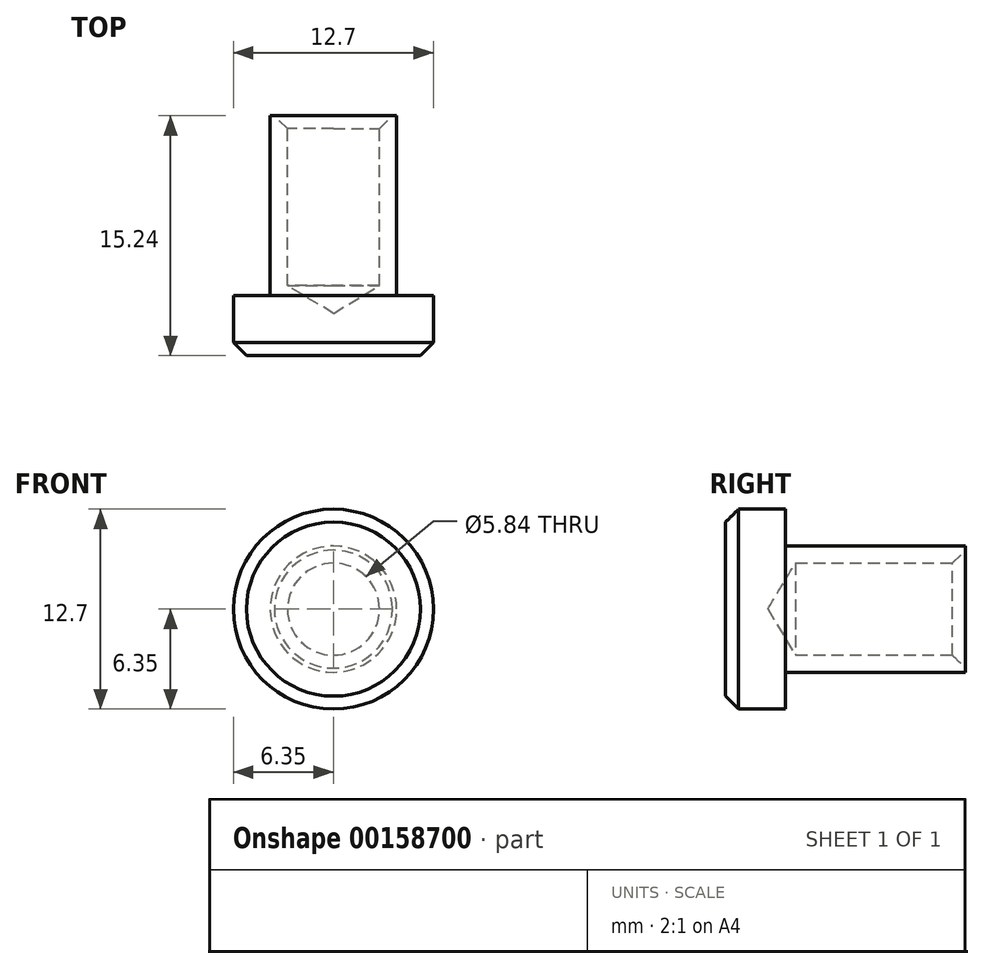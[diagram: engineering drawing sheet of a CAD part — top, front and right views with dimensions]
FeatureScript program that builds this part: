
annotation { "Feature Type Name" : "Feature", "Feature Type Description" : "" }
export const myFeature = defineFeature(function(context is Context, id is Id, definition is map)
    precondition{}
    {
        {
            var Q0;
            Q0=qCreatedBy(makeId("Right.planeOp"),FACE);
            var sketch = newSketch(context, id + "F0", { "sketchPlane" : qUnion([Q0])});
            skLineSegment(sketch, "E0", {"start": v(0, 0) * mm, "end": v(0, 6.35) * mm});
            skLineSegment(sketch, "E1", {"start": v(0, 6.35) * mm, "end": v(3.81, 6.35) * mm});
            skLineSegment(sketch, "E2", {"start": v(3.81, 6.35) * mm, "end": v(3.81, 4.01) * mm});
            skLineSegment(sketch, "E3", {"start": v(3.8, 4.01) * mm, "end": v(15.24, 4.01) * mm});
            skLineSegment(sketch, "E4", {"start": v(15.24, 4.01) * mm, "end": v(15.24, 2.92) * mm});
            skLineSegment(sketch, "E5", {"start": v(15.24, 2.92) * mm, "end": v(4.44, 2.92) * mm});
            skLineSegment(sketch, "E6", {"start": v(4.44, 2.92) * mm, "end": v(2.69, 0) * mm});
            skLineSegment(sketch, "E7", {"start": v(2.69, 0) * mm, "end": v(0, 0) * mm});
            skSolve(sketch);
        }
        {
            var Q0;
            Q0=makeQuery(id+"F0.imprint","IMPRINT",FACE,{"disambiguationData":[TD([[makeQuery(id+"F0.imprint","IMPRINT",EDGE,{"derivedFrom":sQuery(id+"F0.wireOp",EDGE,"E0")}),-1.0]])]});
            var Q1;
            Q1=sQuery(id+"F0.wireOp",EDGE,"E7");
            revolve(context, id + "F1", {"entities" : qUnion([Q0]), "axis" : qUnion([Q1]), "revolveType" : RevolveType.FULL});
        }
        {
            var Q0;
            Q0=makeQuery(id+"F1.opRevolve","SWEPT_EDGE",EDGE,{"disambiguationData":[OSD([sQuery(id+"F0.wireOp",EDGE,"E4"),sQuery(id+"F0.wireOp",EDGE,"E5")])]});
            var Q1;
            Q1=makeQuery(id+"F1.opRevolve","SWEPT_FACE",FACE,{"disambiguationData":[OSD([sQuery(id+"F0.wireOp",EDGE,"E0")])]});
            chamfer(context, id + "F2", {"entities" : qUnion([Q0, Q1]), "width" : 0.83 * mm, "tangentPropagation" : true});
        }
    });
